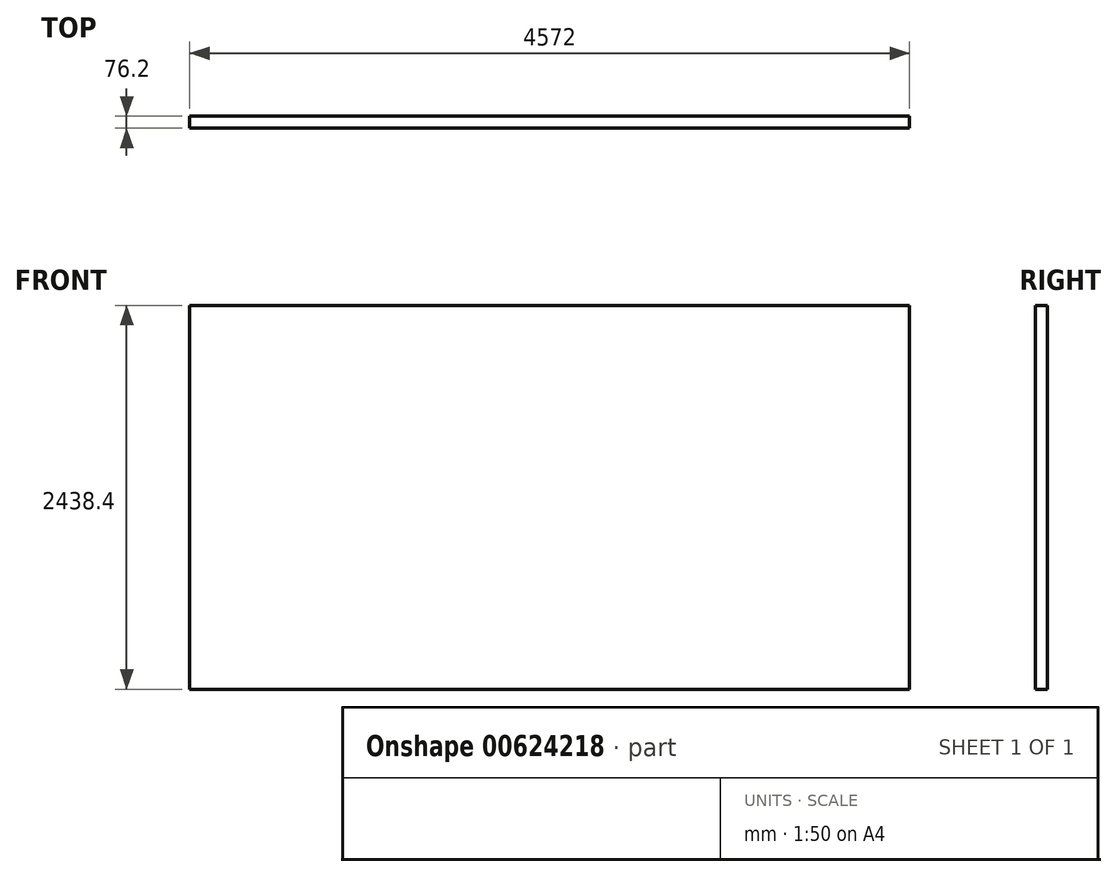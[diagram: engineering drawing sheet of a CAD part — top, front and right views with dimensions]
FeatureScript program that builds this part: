
annotation { "Feature Type Name" : "Feature", "Feature Type Description" : "" }
export const myFeature = defineFeature(function(context is Context, id is Id, definition is map)
    precondition{}
    {
        {
            var Q0;
            Q0=qCreatedBy(makeId("Front.planeOp"),FACE);
            var sketch = newSketch(context, id + "F0", { "sketchPlane" : qUnion([Q0])});
            skLineSegment(sketch, "E0.bottom", {"start": v(-2303.47, 395.39) * mm, "end": v(2268.53, 395.39) * mm});
            skLineSegment(sketch, "E0.top", {"start": v(-2303.47, -2043.01) * mm, "end": v(2268.53, -2043.01) * mm});
            skLineSegment(sketch, "E0.left", {"start": v(-2303.47, 395.39) * mm, "end": v(-2303.47, -2043.01) * mm});
            skLineSegment(sketch, "E0.right", {"start": v(2268.53, 395.39) * mm, "end": v(2268.53, -2043.01) * mm});
            skSolve(sketch);
        }
        {
            var Q0;
            Q0=makeQuery(id+"F0.imprint","IMPRINT",FACE,{"disambiguationData":[TD([[makeQuery(id+"F0.imprint","IMPRINT",EDGE,{"derivedFrom":sQuery(id+"F0.wireOp",EDGE,"E0.bottom")}),-1.0]])]});
            extrude(context, id + "F1", {"entities" : qUnion([Q0]), "depth" : 76.2 * mm, "offsetDistance" : 30.48 * mm});
        }
    });
